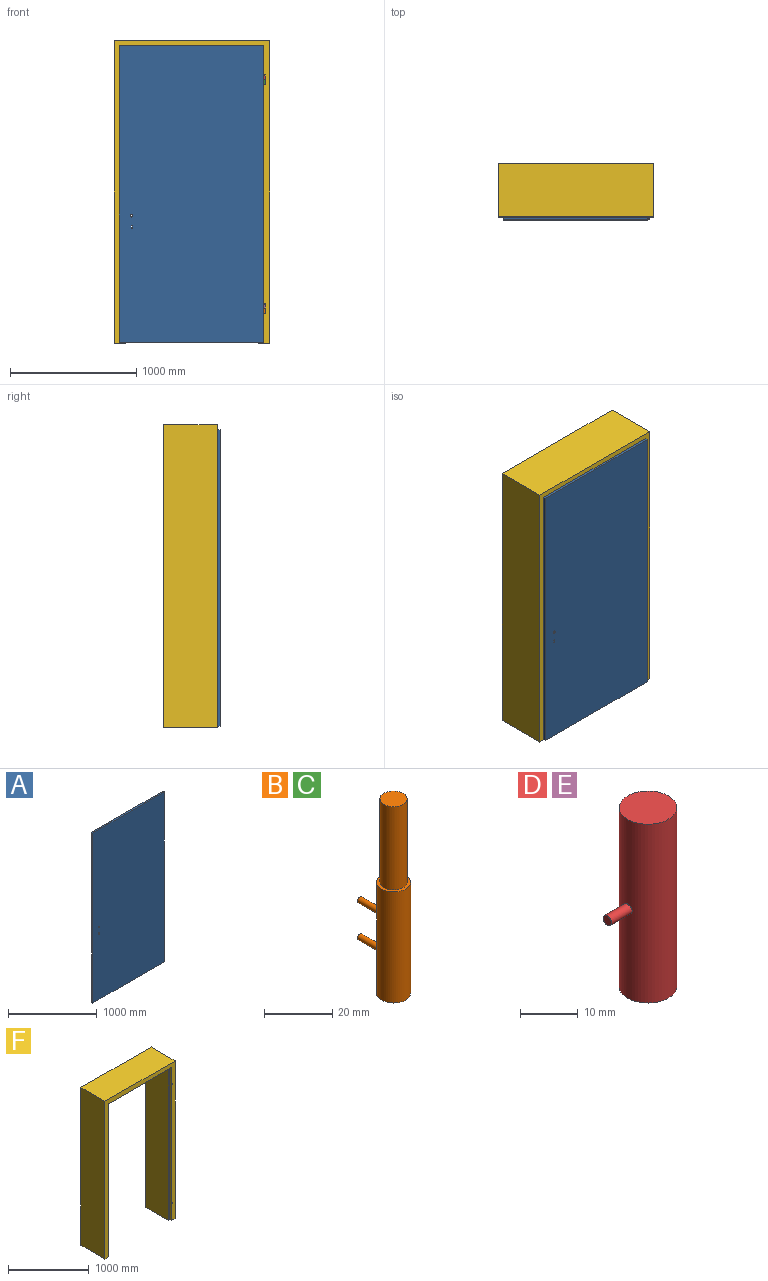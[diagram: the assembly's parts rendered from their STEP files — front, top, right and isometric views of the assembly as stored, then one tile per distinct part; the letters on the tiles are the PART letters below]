
ASSEMBLY  parts=6 mates=5
PART A: 19 faces, bbox 1140x40x2345 mm
  f0: plane 2310x1070mm, normal (0,1,0), area 2471157.3mm2, adj f1,f2,f3,f5,f7,f9,f11,f12
  f1: cylinder r=5mm len=40mm, axis (0,1,0), area 628.3mm2, adj f0,f2,f9,f10
  f2: plane 40x15mm, normal (-1,0,0), area 600mm2, adj f0,f1,f3,f10
  f3: cylinder r=5mm len=40mm, axis (0,1,0), area 628.3mm2, adj f0,f2,f9,f10
  f4: plane 2345x20mm, normal (-1,0,0), area 46900mm2, adj f5,f8,f10,f14
  f5: plane 1140x40mm, normal (0,0,-1), area 44200mm2, adj f0,f4,f6,f10,f11,f13,f14
  f6: plane 2345x20mm, normal (1,0,0), area 46893.7mm2, adj f5,f8,f10,f14,f15,f17
  f7: cylinder r=10mm len=40mm, axis (0,1,0), area 2513.3mm2, adj f0,f10
  f8: plane 1140x20mm, normal (0,0,1), area 22800mm2, adj f4,f6,f10,f14
  f9: plane 40x15mm, normal (1,0,0), area 600mm2, adj f0,f1,f3,f10
  f10: plane 2345x1140mm, normal (0,-1,0), area 2672757.3mm2, adj f1,f2,f3,f4,f5,f6,f7,f8
  f11: plane 2310x20mm, normal (-1,0,0), area 46200mm2, adj f0,f5,f12,f14
  f12: plane 1070x20mm, normal (0,0,1), area 21400mm2, adj f0,f11,f13,f14
  f13: plane 2310x20mm, normal (1,0,0), area 46200mm2, adj f0,f5,f12,f14
  f14: plane 2345x1140mm, normal (0,1,0), area 201600mm2, adj f4,f5,f6,f8,f11,f12,f13
  f15: cylinder r=1mm len=10mm, axis (1,0,0), area 62.8mm2, adj f6,f16
  f16: plane 2x2mm, normal (1,0,0), area 3.1mm2, adj f15
  f17: cylinder r=1mm len=10mm, axis (1,0,0), area 62.8mm2, adj f6,f18
  f18: plane 2x2mm, normal (1,0,0), area 3.1mm2, adj f17
PART B: 9 faces, bbox 10x19x70 mm
  f0: cylinder r=4mm len=30mm, axis (0,0,-1), area 754mm2, adj f1,f4
  f1: plane 8x8mm, normal (0,0,1), area 50.3mm2, adj f0
  f2: cylinder r=5mm len=40mm, axis (0,0,1), area 1250.3mm2, adj f3,f4,f5,f7
  f3: plane 10x10mm, normal (0,0,-1), area 78.5mm2, adj f2
  f4: plane 10x10mm, normal (0,0,1), area 28.3mm2, adj f0,f2
  f5: cylinder r=1mm len=9.1mm, axis (0,-1,0), area 56.9mm2, adj f2,f6
  f6: plane 2x2mm, normal (0,1,0), area 3.1mm2, adj f5
  f7: cylinder r=1mm len=9.1mm, axis (0,-1,0), area 56.9mm2, adj f2,f8
  f8: plane 2x2mm, normal (0,1,0), area 3.1mm2, adj f7
PART C: same geometry as B
PART D: 7 faces, bbox 15x10x38 mm
  f0: cylinder r=4mm len=35mm, axis (0,0,1), area 879.6mm2, adj f2,f3
  f1: cylinder r=5mm len=38mm, axis (0,0,1), area 1190.6mm2, adj f2,f4,f6
  f2: plane 10x10mm, normal (0,0,-1), area 28.3mm2, adj f0,f1
  f3: plane 8x8mm, normal (0,0,-1), area 50.3mm2, adj f0
  f4: plane 10x10mm, normal (0,0,1), area 78.5mm2, adj f1
  f5: plane 2x2mm, normal (-1,0,0), area 3.1mm2, adj f6
  f6: cylinder r=1mm len=5.1mm, axis (1,0,0), area 31.7mm2, adj f1,f5
PART E: same geometry as D
PART F: 29 faces, bbox 1230x420x2390 mm
  f0: plane 2318x1086mm, normal (0,-1,0), area 102344.1mm2, adj f1,f2,f3,f4,f6,f14,f15,f16
  f1: plane 420x90mm, normal (0,0,-1), area 37300.9mm2, adj f0,f2,f5,f9,f10,f13,f16
  f2: plane 2300x395mm, normal (1,0,0), area 908500mm2, adj f0,f1,f3,f10
  f3: plane 1050x395mm, normal (0,0,-1), area 414750mm2, adj f0,f2,f4,f10
  f4: plane 2300x395mm, normal (-1,0,0), area 908500mm2, adj f0,f3,f6,f10
  f5: plane 2390x1230mm, normal (0,-1,0), area 410898.2mm2, adj f1,f6,f7,f8,f9,f11,f12,f13
  f6: plane 420x90mm, normal (0,0,-1), area 37300.9mm2, adj f0,f4,f5,f7,f10,f11,f14
  f7: plane 2390x420mm, normal (1,0,0), area 1003800mm2, adj f5,f6,f8,f10
  f8: plane 1230x420mm, normal (0,0,1), area 516600mm2, adj f5,f7,f9,f10
  f9: plane 2390x420mm, normal (-1,0,0), area 1003800mm2, adj f1,f5,f8,f10
  f10: plane 2390x1230mm, normal (0,1,0), area 524700mm2, adj f1,f2,f3,f4,f6,f7,f8,f9
  f11: plane 2315x23mm, normal (-1,0,0), area 53245mm2, adj f5,f6,f14,f19
  f12: plane 1080x23mm, normal (0,0,-1), area 24840mm2, adj f5,f15,f17,f19
  f13: plane 2315x23mm, normal (1,0,0), area 53245mm2, adj f1,f5,f16,f17
  f14: cylinder r=2mm len=2315mm, axis (0,0,1), area 7272.8mm2, adj f0,f6,f11,f20
  f15: cylinder r=2mm len=1080mm, axis (-1,0,0), area 3392.9mm2, adj f0,f12,f18,f20
  f16: cylinder r=2mm len=2315mm, axis (0,0,-1), area 7272.8mm2, adj f0,f1,f13,f18
  f17: cylinder r=5mm len=23mm, axis (0,-1,0), area 180.6mm2, adj f5,f12,f13,f18
  f18: torus R=3mm, axis (0,-1,0), area 21.1mm2, adj f0,f15,f16,f17
  f19: cylinder r=5mm len=23mm, axis (0,1,0), area 180.6mm2, adj f5,f11,f12,f20
  f20: torus R=3mm, axis (0,-1,0), area 21.1mm2, adj f0,f14,f15,f19
  f21: cylinder r=1mm len=12mm, axis (0,-1,0), area 75.4mm2, adj f5,f22
  f22: plane 2x2mm, normal (0,-1,0), area 3.1mm2, adj f21
  f23: cylinder r=1mm len=12mm, axis (0,-1,0), area 75.4mm2, adj f5,f24
  f24: plane 2x2mm, normal (0,-1,0), area 3.1mm2, adj f23
  f25: cylinder r=1mm len=12mm, axis (0,-1,0), area 75.4mm2, adj f5,f26
  f26: plane 2x2mm, normal (0,-1,0), area 3.1mm2, adj f25
  f27: cylinder r=1mm len=12mm, axis (0,-1,0), area 75.4mm2, adj f5,f28
  f28: plane 2x2mm, normal (0,-1,0), area 3.1mm2, adj f27
PLACE A rot(axis=(0.01,0,1),0deg) t=(73,-4,7)mm
PLACE B t=(1188,-14,276.67)mm
PLACE C t=(1188,-14,2083.33)mm
PLACE D rot(axis=(0,0,1),0deg) t=(1188,-14,2118.33)mm
PLACE E rot(axis=(0,0,1),0deg) t=(1188,-14,312)mm
PLACE F at identity fixed
MATE fastened D.f6 <-> A.f17  axis (-1,0,0) through (1178,-14,2102.33)mm
MATE fastened A.f15 <-> E.f6  axis (1,0,0) through (1178,-14,296)mm
MATE fastened B.f5 <-> F.f23  axis (0,1,0) through (1188,0,263.33)mm
MATE fastened C.f5 <-> F.f27  axis (0,1,0) through (1188,0,2070)mm
MATE revolute D.f1 <-> C.f2  axis (0,0,1) through (1188,-14,2083.33)mm
